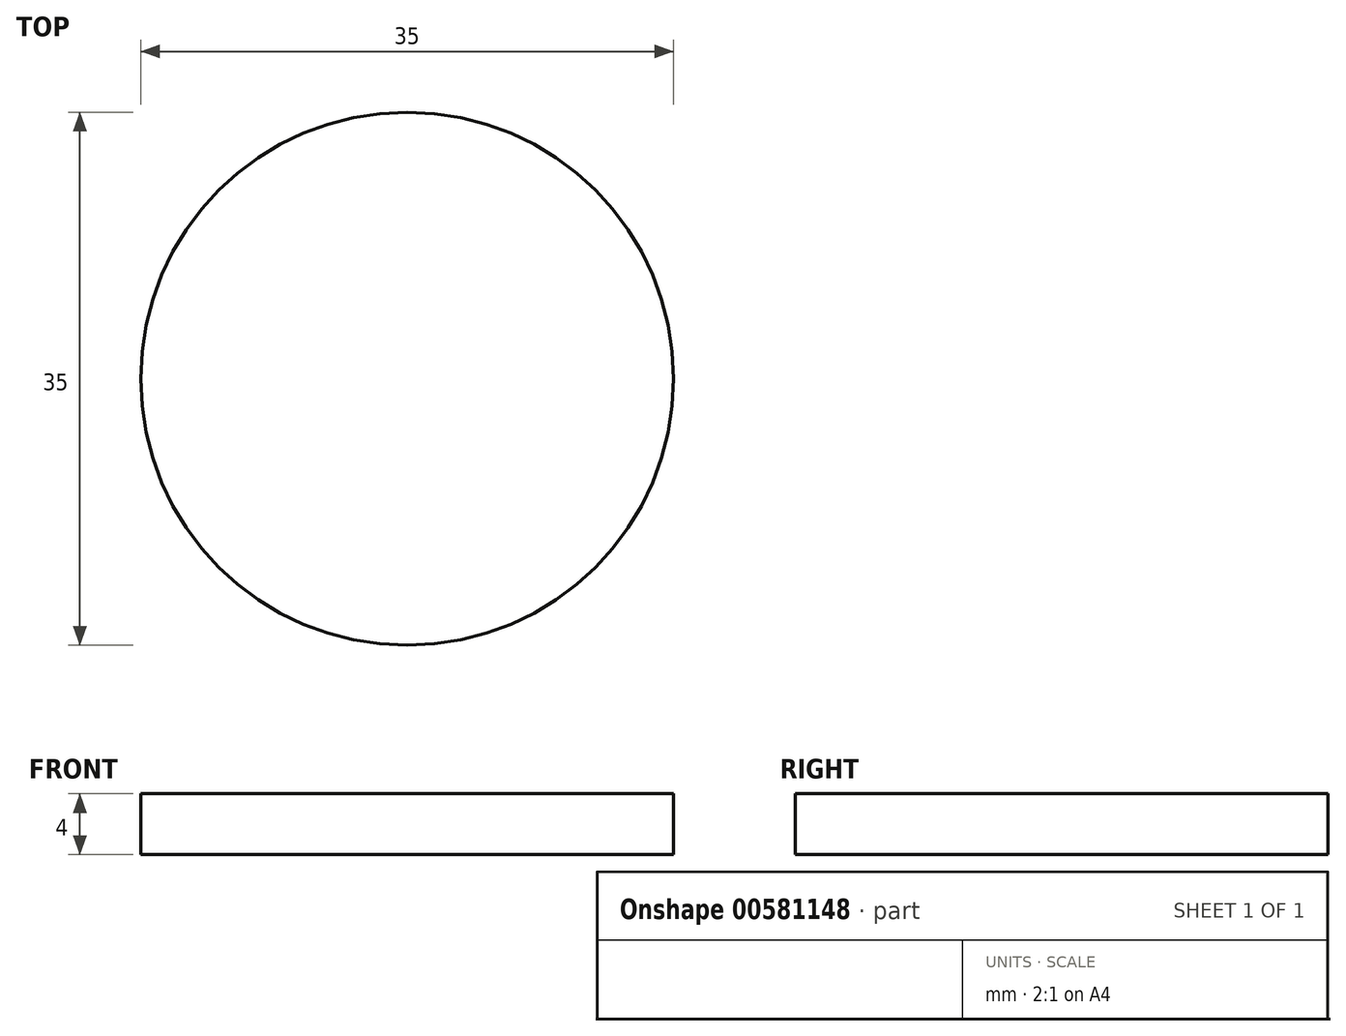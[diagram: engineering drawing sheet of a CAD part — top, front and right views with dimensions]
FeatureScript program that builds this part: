
annotation { "Feature Type Name" : "Feature", "Feature Type Description" : "" }
export const myFeature = defineFeature(function(context is Context, id is Id, definition is map)
    precondition{}
    {
        {
            var Q0;
            Q0=qCreatedBy(makeId("Top.planeOp"),FACE);
            var sketch = newSketch(context, id + "F0", { "sketchPlane" : qUnion([Q0])});
            skCircle(sketch, "E0", {"center": v(0, 0) * mm, "radius": 17.5 * mm});
            skSolve(sketch);
        }
        {
            var Q0;
            Q0=qSketchRegion(id+"F0",true);
            extrude(context, id + "F1", {"entities" : qUnion([Q0]), "depth" : 4 * mm, "offsetDistance" : 25 * mm});
        }
    });
